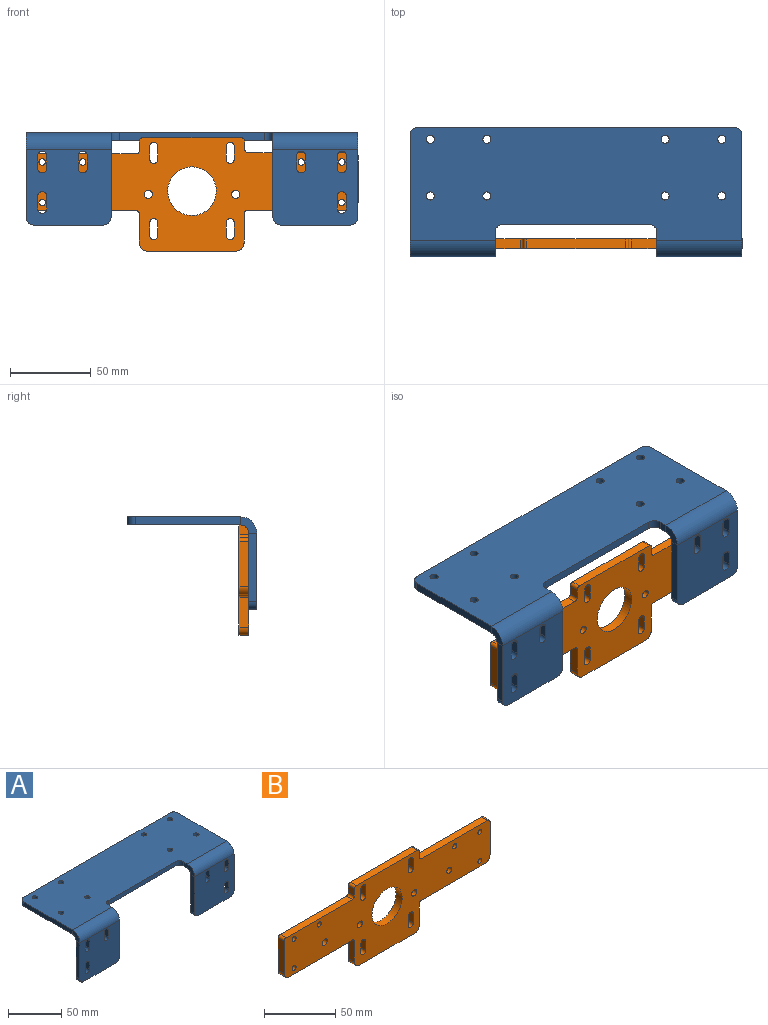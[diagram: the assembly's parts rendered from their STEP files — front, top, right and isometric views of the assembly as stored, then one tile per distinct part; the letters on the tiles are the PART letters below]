
ASSEMBLY  parts=2 mates=1
PART A: 66 faces, bbox 205x80x57 mm
  f0: plane 42x5mm, normal (1,0,0), area 210mm2, adj f15,f16,f18,f62
  f1: plane 42x5mm, normal (-1,0,0), area 210mm2, adj f15,f16,f17,f63
  f2: cylinder r=2.75mm len=5.5mm, axis (0,-1,0), area 43.2mm2, adj f3,f13,f15,f16
  f3: plane 8x5mm, normal (1,0,0), area 40mm2, adj f2,f4,f15,f16
  f4: cylinder r=2.75mm len=5.5mm, axis (0,-1,0), area 43.2mm2, adj f3,f13,f15,f16
  f5: cylinder r=2.75mm len=5.5mm, axis (0,-1,0), area 43.2mm2, adj f6,f12,f15,f16
  f6: plane 8x5mm, normal (-1,0,0), area 40mm2, adj f5,f7,f15,f16
  f7: cylinder r=2.75mm len=5.5mm, axis (0,-1,0), area 43.2mm2, adj f6,f12,f15,f16
  f8: cylinder r=2.75mm len=5.5mm, axis (0,-1,0), area 43.2mm2, adj f9,f11,f15,f16
  f9: plane 8x5mm, normal (1,0,0), area 40mm2, adj f8,f10,f15,f16
  f10: cylinder r=2.75mm len=5.5mm, axis (0,-1,0), area 43.2mm2, adj f9,f11,f15,f16
  f11: plane 8x5mm, normal (-1,0,0), area 40mm2, adj f8,f10,f15,f16
  f12: plane 8x5mm, normal (1,0,0), area 40mm2, adj f5,f7,f15,f16
  f13: plane 8x5mm, normal (-1,0,0), area 40mm2, adj f2,f4,f15,f16
  f14: plane 42.5x5mm, normal (0,0,-1), area 212.5mm2, adj f15,f16,f17,f18
  f15: plane 52.5x47mm, normal (0,-1,0), area 2253.5mm2, adj f0,f1,f2,f3,f4,f5,f6,f7
  f16: plane 52.5x47mm, normal (0,1,0), area 2253.5mm2, adj f0,f1,f2,f3,f4,f5,f6,f7
  f17: cylinder r=5mm len=5mm, axis (0,1,0), area 39.3mm2, adj f1,f14,f15,f16
  f18: cylinder r=5mm len=5mm, axis (0,1,0), area 39.3mm2, adj f0,f14,f15,f16
  f19: plane 42x5mm, normal (1,0,0), area 210mm2, adj f34,f35,f36,f58
  f20: plane 42x5mm, normal (-1,0,0), area 210mm2, adj f34,f35,f37,f59
  f21: cylinder r=2.75mm len=5.5mm, axis (0,-1,0), area 43.2mm2, adj f22,f32,f34,f35
  f22: plane 8x5mm, normal (1,0,0), area 40mm2, adj f21,f23,f34,f35
  f23: cylinder r=2.75mm len=5.5mm, axis (0,-1,0), area 43.2mm2, adj f22,f32,f34,f35
  f24: cylinder r=2.75mm len=5.5mm, axis (0,-1,0), area 43.2mm2, adj f25,f31,f34,f35
  f25: plane 8x5mm, normal (-1,0,0), area 40mm2, adj f24,f26,f34,f35
  f26: cylinder r=2.75mm len=5.5mm, axis (0,-1,0), area 43.2mm2, adj f25,f31,f34,f35
  f27: cylinder r=2.75mm len=5.5mm, axis (0,-1,0), area 43.2mm2, adj f28,f30,f34,f35
  f28: plane 8x5mm, normal (1,0,0), area 40mm2, adj f27,f29,f34,f35
  f29: cylinder r=2.75mm len=5.5mm, axis (0,-1,0), area 43.2mm2, adj f28,f30,f34,f35
  f30: plane 8x5mm, normal (-1,0,0), area 40mm2, adj f27,f29,f34,f35
  f31: plane 8x5mm, normal (1,0,0), area 40mm2, adj f24,f26,f34,f35
  f32: plane 8x5mm, normal (-1,0,0), area 40mm2, adj f21,f23,f34,f35
  f33: plane 42.5x5mm, normal (0,0,-1), area 212.5mm2, adj f34,f35,f36,f37
  f34: plane 52.5x47mm, normal (0,-1,0), area 2253.5mm2, adj f19,f20,f21,f22,f23,f24,f25,f26
  f35: plane 52.5x47mm, normal (0,1,0), area 2253.5mm2, adj f19,f20,f21,f22,f23,f24,f25,f26
  f36: cylinder r=5mm len=5mm, axis (0,-1,0), area 39.3mm2, adj f19,f33,f34,f35
  f37: cylinder r=5mm len=5mm, axis (0,-1,0), area 39.3mm2, adj f20,f33,f34,f35
  f38: plane 65x5mm, normal (1,0,0), area 325mm2, adj f54,f55,f56,f58
  f39: plane 195x5mm, normal (0,1,0), area 975mm2, adj f54,f55,f56,f57
  f40: plane 65x5mm, normal (-1,0,0), area 325mm2, adj f54,f55,f57,f63
  f41: plane 5x5mm, normal (1,0,0), area 25mm2, adj f42,f54,f55,f62
  f42: cylinder r=5mm len=5mm, axis (0,0,1), area 39.3mm2, adj f41,f43,f54,f55
  f43: plane 90x5mm, normal (0,-1,0), area 450mm2, adj f42,f44,f54,f55
  f44: cylinder r=5mm len=5mm, axis (0,0,1), area 39.3mm2, adj f43,f53,f54,f55
  f45: cylinder r=2.5mm len=5mm, axis (0,0,1), area 78.5mm2, adj f54,f55
  f46: cylinder r=2.5mm len=5mm, axis (0,0,1), area 78.5mm2, adj f54,f55
  f47: cylinder r=2.5mm len=5mm, axis (0,0,1), area 78.5mm2, adj f54,f55
  f48: cylinder r=2.5mm len=5mm, axis (0,0,1), area 78.5mm2, adj f54,f55
  f49: cylinder r=2.5mm len=5mm, axis (0,0,1), area 78.5mm2, adj f54,f55
  f50: cylinder r=2.5mm len=5mm, axis (0,0,1), area 78.5mm2, adj f54,f55
  f51: cylinder r=2.5mm len=5mm, axis (0,0,1), area 78.5mm2, adj f54,f55
  f52: cylinder r=2.5mm len=5mm, axis (0,0,1), area 78.5mm2, adj f54,f55
  f53: plane 5x5mm, normal (-1,0,0), area 25mm2, adj f44,f54,f55,f59
  f54: plane 205x70mm, normal (0,0,1), area 13192.9mm2, adj f38,f39,f40,f41,f42,f43,f44,f45
  f55: plane 205x70mm, normal (0,0,-1), area 13192.9mm2, adj f38,f39,f40,f41,f42,f43,f44,f45
  f56: cylinder r=5mm len=5mm, axis (0,0,-1), area 39.3mm2, adj f38,f39,f54,f55
  f57: cylinder r=5mm len=5mm, axis (0,0,1), area 39.3mm2, adj f39,f40,f54,f55
  f58: plane 10x10mm, normal (1,0,0), area 58.9mm2, adj f19,f38,f60,f61
  f59: plane 10x10mm, normal (-1,0,0), area 58.9mm2, adj f20,f53,f60,f61
  f60: cylinder r=10mm len=52.5mm, axis (1,0,0), area 824.7mm2, adj f34,f54,f58,f59
  f61: cylinder r=5mm len=52.5mm, axis (1,0,0), area 412.3mm2, adj f35,f55,f58,f59
  f62: plane 10x10mm, normal (1,0,0), area 58.9mm2, adj f0,f41,f64,f65
  f63: plane 10x10mm, normal (-1,0,0), area 58.9mm2, adj f1,f40,f64,f65
  f64: cylinder r=10mm len=52.5mm, axis (1,0,0), area 824.7mm2, adj f15,f54,f62,f63
  f65: cylinder r=5mm len=52.5mm, axis (1,0,0), area 412.3mm2, adj f16,f55,f62,f63
PART B: 53 faces, bbox 205x6x70 mm
  f0: cylinder r=2.5mm len=6mm, axis (0,1,0), area 47.1mm2, adj f1,f46,f47,f48
  f1: plane 8x6mm, normal (1,0,0), area 48mm2, adj f0,f2,f47,f48
  f2: cylinder r=2.5mm len=6mm, axis (0,1,0), area 47.1mm2, adj f1,f46,f47,f48
  f3: cylinder r=2.5mm len=6mm, axis (0,1,0), area 47.1mm2, adj f4,f31,f47,f48
  f4: plane 8x6mm, normal (1,0,0), area 48mm2, adj f3,f5,f47,f48
  f5: cylinder r=2.5mm len=6mm, axis (0,1,0), area 47.1mm2, adj f4,f31,f47,f48
  f6: cylinder r=2.5mm len=6mm, axis (0,1,0), area 47.1mm2, adj f7,f32,f47,f48
  f7: plane 8x6mm, normal (1,0,0), area 48mm2, adj f6,f8,f47,f48
  f8: cylinder r=2.5mm len=6mm, axis (0,1,0), area 47.1mm2, adj f7,f32,f47,f48
  f9: plane 66x6mm, normal (0,0,1), area 396mm2, adj f10,f33,f47,f48
  f10: cylinder r=2mm len=6mm, axis (0,1,0), area 18.8mm2, adj f9,f11,f47,f48
  f11: plane 28x6mm, normal (-1,0,0), area 168mm2, adj f10,f47,f48,f49
  f12: plane 63x6mm, normal (0,0,-1), area 378mm2, adj f13,f47,f48,f49
  f13: cylinder r=2mm len=6mm, axis (0,1,0), area 18.8mm2, adj f12,f14,f47,f48
  f14: plane 18x6mm, normal (-1,0,0), area 108mm2, adj f13,f47,f48,f50
  f15: plane 54.61x6mm, normal (0,0,-1), area 327.7mm2, adj f47,f48,f50,f51
  f16: plane 18x6mm, normal (1,0,0), area 108mm2, adj f17,f47,f48,f51
  f17: cylinder r=2mm len=6mm, axis (0,1,0), area 18.8mm2, adj f16,f18,f47,f48
  f18: plane 63.39x6mm, normal (0,0,-1), area 380.3mm2, adj f17,f47,f48,f52
  f19: plane 28.77x6mm, normal (1,0,0), area 172.6mm2, adj f20,f47,f48,f52
  f20: cylinder r=2mm len=6mm, axis (0,1,0), area 18.8mm2, adj f19,f21,f47,f48
  f21: plane 66x6mm, normal (0,0,1), area 396mm2, adj f20,f22,f47,f48
  f22: cylinder r=2mm len=6mm, axis (0,1,0), area 18.8mm2, adj f21,f23,f47,f48
  f23: plane 6x5.24mm, normal (1,0,0), area 31.4mm2, adj f22,f24,f47,f48
  f24: cylinder r=2mm len=6mm, axis (0,1,0), area 18.8mm2, adj f23,f25,f47,f48
  f25: plane 61x6mm, normal (0,0,1), area 366mm2, adj f24,f26,f47,f48
  f26: cylinder r=2mm len=6mm, axis (0,1,0), area 18.8mm2, adj f25,f27,f47,f48
  f27: plane 6x6mm, normal (-1,0,0), area 36mm2, adj f26,f33,f47,f48
  f28: cylinder r=2.5mm len=6mm, axis (0,1,0), area 47.1mm2, adj f29,f45,f47,f48
  f29: plane 8x6mm, normal (1,0,0), area 48mm2, adj f28,f30,f47,f48
  f30: cylinder r=2.5mm len=6mm, axis (0,1,0), area 47.1mm2, adj f29,f45,f47,f48
  f31: plane 8x6mm, normal (-1,0,0), area 48mm2, adj f3,f5,f47,f48
  f32: plane 8x6mm, normal (-1,0,0), area 48mm2, adj f6,f8,f47,f48
  f33: cylinder r=2mm len=6mm, axis (0,1,0), area 18.8mm2, adj f9,f27,f47,f48
  f34: cylinder r=2.5mm len=6mm, axis (0,1,0), area 94.2mm2, adj f47,f48
  f35: cylinder r=2.5mm len=6mm, axis (0,1,0), area 94.2mm2, adj f47,f48
  f36: cylinder r=2.5mm len=6mm, axis (0,1,0), area 94.2mm2, adj f47,f48
  f37: cylinder r=2.5mm len=6mm, axis (0,1,0), area 94.2mm2, adj f47,f48
  f38: cylinder r=15mm len=30mm, axis (0,1,0), area 565.5mm2, adj f47,f48
  f39: cylinder r=2mm len=6mm, axis (0,1,0), area 75.4mm2, adj f47,f48
  f40: cylinder r=2mm len=6mm, axis (0,1,0), area 75.4mm2, adj f47,f48
  f41: cylinder r=2mm len=6mm, axis (0,1,0), area 75.4mm2, adj f47,f48
  f42: cylinder r=2mm len=6mm, axis (0,1,0), area 75.4mm2, adj f47,f48
  f43: cylinder r=2mm len=6mm, axis (0,1,0), area 75.4mm2, adj f47,f48
  f44: cylinder r=2mm len=6mm, axis (0,1,0), area 75.4mm2, adj f47,f48
  f45: plane 8x6mm, normal (-1,0,0), area 48mm2, adj f28,f30,f47,f48
  f46: plane 8x6mm, normal (-1,0,0), area 48mm2, adj f0,f2,f47,f48
  f47: plane 205x70mm, normal (0,-1,0), area 8373.1mm2, adj f0,f1,f2,f3,f4,f5,f6,f7
  f48: plane 205x70mm, normal (0,1,0), area 8373.1mm2, adj f0,f1,f2,f3,f4,f5,f6,f7
  f49: cylinder r=5mm len=6mm, axis (0,-1,0), area 47.1mm2, adj f11,f12,f47,f48
  f50: cylinder r=5mm len=6mm, axis (0,-1,0), area 47.1mm2, adj f14,f15,f47,f48
  f51: cylinder r=5mm len=6mm, axis (0,1,0), area 47.1mm2, adj f15,f16,f47,f48
  f52: cylinder r=5mm len=6mm, axis (0,-1,0), area 47.1mm2, adj f18,f19,f47,f48
PLACE A t=(-56.84,45.82,-83.09)mm
PLACE B t=(-14.91,-23.18,-57.97)mm
MATE fastened B.f43 <-> A.f16  axis (0,-1,0) through (-21.84,-29.18,-21.09)mm
